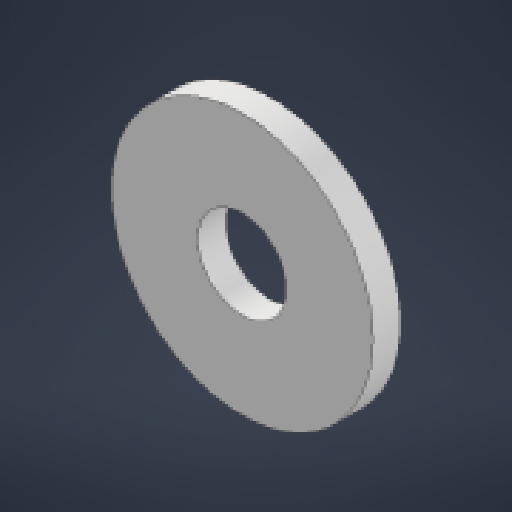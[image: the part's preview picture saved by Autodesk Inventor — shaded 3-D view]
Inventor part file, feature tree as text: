
AUTODESK INVENTOR PART (.ipt)
format: ipt  version: 2024.1 (Build 281209000, 209)  size: 119,808 bytes
history: native  units: in
note: dims shown in document units (in); Inventor stores cm internally (conversion verified against a paired STEP export)
features: extrude x1, sketch x1
ambient origin geometry x8: Origin, YZ Plane, XZ Plane, XY Plane, X Axis, Y Axis, Z Axis, Center Point
bodies: Solid1 (feature_tree)
feature tree (2):
  extrude  "Extrusion1"  Depth=0.63in
  sketch  "Sketch1"  dims[d0=5.91in d1=2.0in d2=0.63in d3=0.0in]
